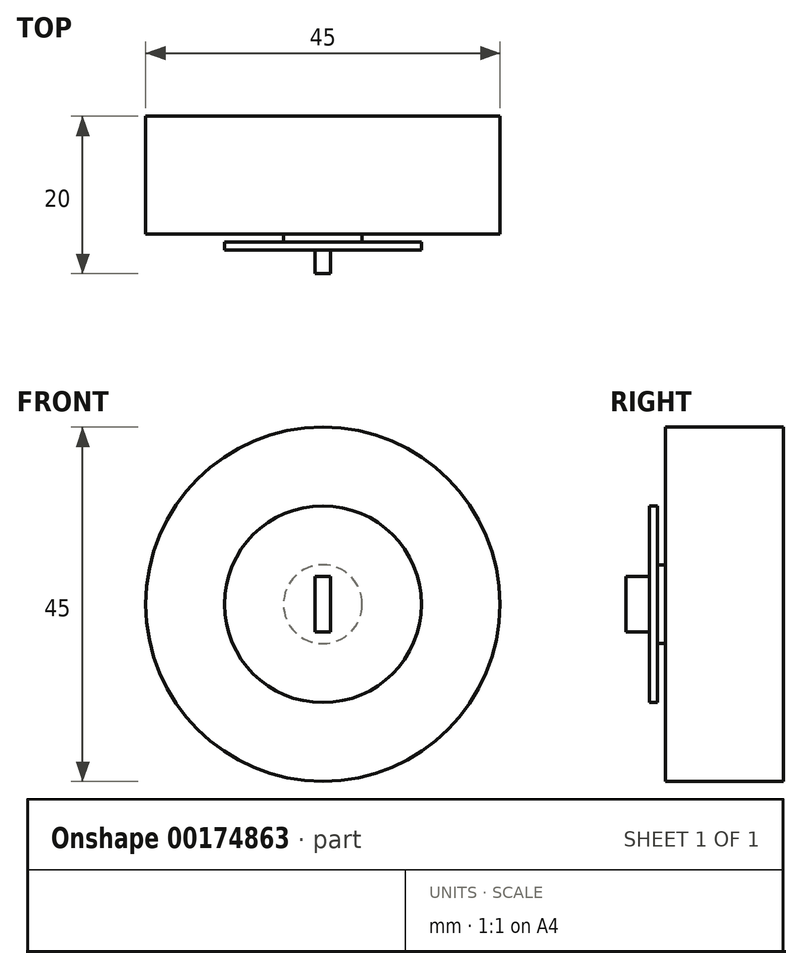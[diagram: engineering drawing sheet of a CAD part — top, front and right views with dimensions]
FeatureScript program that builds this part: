
annotation { "Feature Type Name" : "Feature", "Feature Type Description" : "" }
export const myFeature = defineFeature(function(context is Context, id is Id, definition is map)
    precondition{}
    {
        {
            var Q0;
            Q0=qCreatedBy(makeId("Front.planeOp"),FACE);
            var sketch = newSketch(context, id + "F0", { "sketchPlane" : qUnion([Q0])});
            skCircle(sketch, "E0", {"center": v(0, 0) * mm, "radius": 12.5 * mm});
            skSolve(sketch);
        }
        {
            var Q0;
            Q0 = qSketchRegion(id + "F0", true);
            extrude(context, id + "F1", {"entities" : qUnion([Q0]), "depth" : 1 * mm});
        }
        {
            var Q0;
            Q0=makeQuery(id+"F1.opExtrude","CAP_FACE",FACE,{"disambiguationData":[OSD([sQuery(id+"F0.wireOp",EDGE,"E0")])],"isStart":false});
            var sketch = newSketch(context, id + "F2", { "sketchPlane" : qUnion([Q0])});
            skLineSegment(sketch, "E1.bottom", {"start": v(1, 3.5) * mm, "end": v(-1, 3.5) * mm});
            skLineSegment(sketch, "E1.top", {"start": v(1, -3.5) * mm, "end": v(-1, -3.5) * mm});
            skLineSegment(sketch, "E1.left", {"start": v(1, 3.5) * mm, "end": v(1, -3.5) * mm});
            skLineSegment(sketch, "E1.right", {"start": v(-1, 3.5) * mm, "end": v(-1, -3.5) * mm});
            skPoint(sketch, "E1.middle", {"position": v(0, 0) * mm});
            skSolve(sketch);
        }
        {
            var Q0;
            Q0 = qSketchRegion(id + "F2", true);
            extrude(context, id + "F3", {"entities" : qUnion([Q0]), "operationType" : NewBodyOperationType.ADD, "depth" : 3 * mm});
        }
        {
            var Q0;
            Q0=makeQuery(id+"F1.opExtrude","CAP_FACE",FACE,{"disambiguationData":[OSD([sQuery(id+"F0.wireOp",EDGE,"E0")])],"isStart":true});
            var sketch = newSketch(context, id + "F4", { "sketchPlane" : qUnion([Q0])});
            skCircle(sketch, "E2", {"center": v(0, 0) * mm, "radius": 5 * mm});
            skSolve(sketch);
        }
        {
            var Q0;
            Q0 = qSketchRegion(id + "F4", true);
            extrude(context, id + "F5", {"entities" : qUnion([Q0]), "operationType" : NewBodyOperationType.ADD, "depth" : 1 * mm});
        }
        {
            var Q0;
            Q0=makeQuery(id+"F5.opExtrude","CAP_FACE",FACE,{"disambiguationData":[OSD([sQuery(id+"F4.wireOp",EDGE,"E2")])],"isStart":false});
            var sketch = newSketch(context, id + "F6", { "sketchPlane" : qUnion([Q0])});
            skCircle(sketch, "E3", {"center": v(0, 0) * mm, "radius": 22.5 * mm});
            skSolve(sketch);
        }
        {
            var Q0;
            Q0 = qSketchRegion(id + "F6", true);
            extrude(context, id + "F7", {"entities" : qUnion([Q0]), "operationType" : NewBodyOperationType.ADD, "depth" : 15 * mm});
        }
    });
